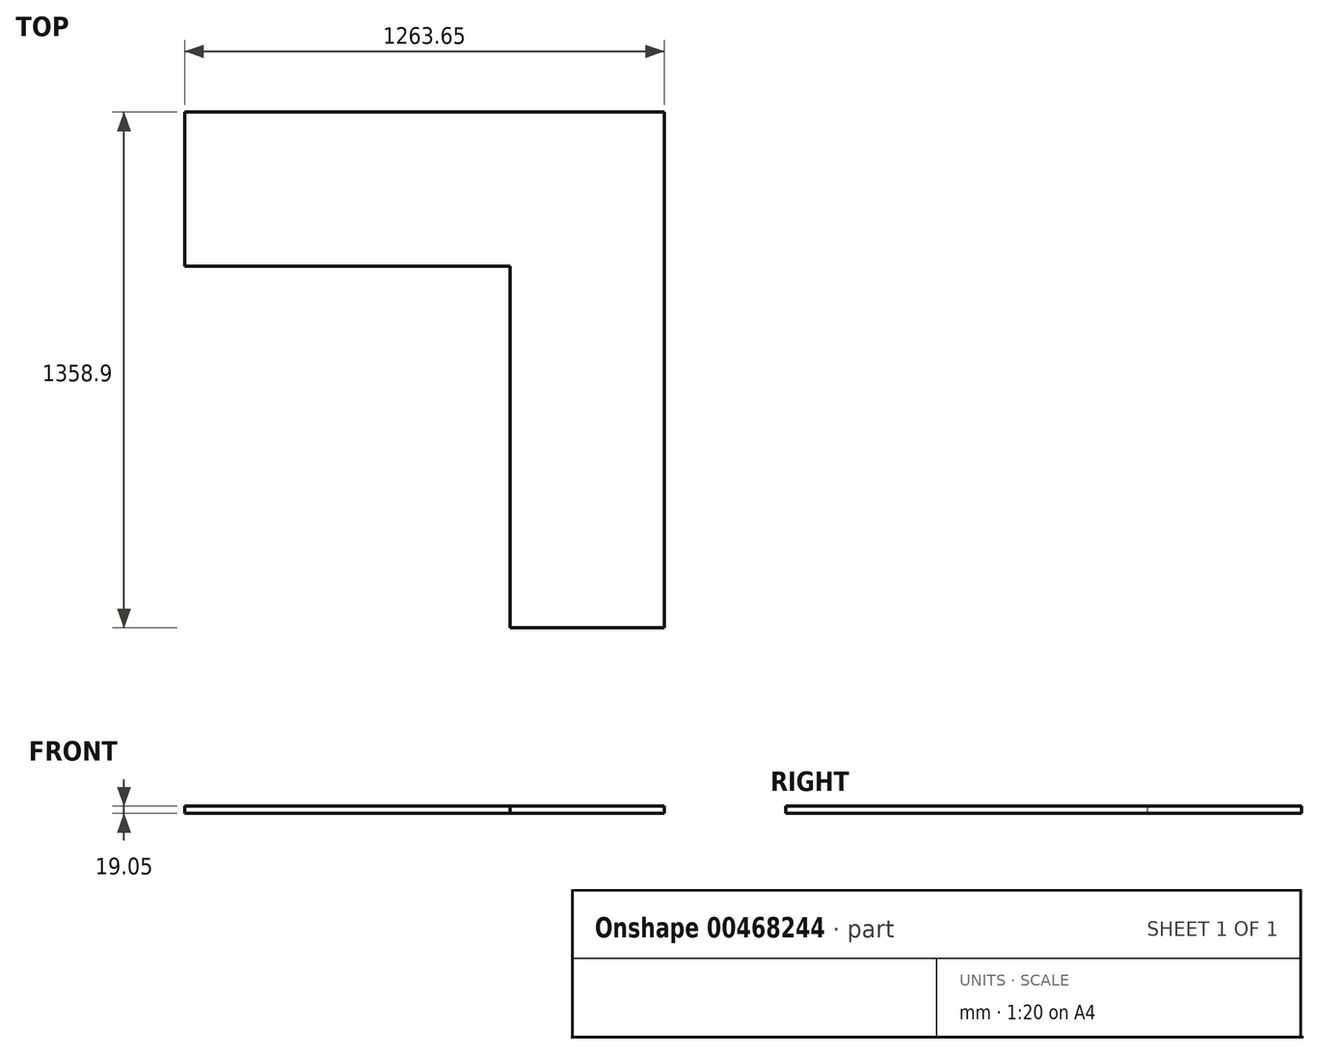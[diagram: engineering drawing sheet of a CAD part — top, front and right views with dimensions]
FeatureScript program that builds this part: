
annotation { "Feature Type Name" : "Feature", "Feature Type Description" : "" }
export const myFeature = defineFeature(function(context is Context, id is Id, definition is map)
    precondition{}
    {
        {
            var Q0;
            Q0=qCreatedBy(makeId("Top.planeOp"),FACE);
            var sketch = newSketch(context, id + "F0", { "sketchPlane" : qUnion([Q0])});
            skLineSegment(sketch, "E0", {"start": v(0, 0) * mm, "end": v(-1263.65, 0) * mm});
            skLineSegment(sketch, "E1", {"start": v(-1263.65, 0) * mm, "end": v(-1263.65, -406.4) * mm});
            skLineSegment(sketch, "E2", {"start": v(-406.4, -1358.9) * mm, "end": v(0, -1358.9) * mm});
            skLineSegment(sketch, "E3", {"start": v(0, -1358.9) * mm, "end": v(0, 0) * mm});
            skLineSegment(sketch, "E4", {"start": v(-1263.65, -406.4) * mm, "end": v(-406.4, -406.4) * mm});
            skLineSegment(sketch, "E5", {"start": v(-406.4, -406.4) * mm, "end": v(-406.4, -1358.9) * mm});
            skLineSegment(sketch, "E6.0", {"start": v(-1225.55, -38.1) * mm, "end": v(-1225.55, -406.4) * mm});
            skLineSegment(sketch, "E6.1", {"start": v(-38.1, -38.1) * mm, "end": v(-1225.55, -38.1) * mm});
            skLineSegment(sketch, "E6.2", {"start": v(-38.1, -1320.8) * mm, "end": v(-38.1, -38.1) * mm});
            skLineSegment(sketch, "E6.3", {"start": v(-406.4, -1320.8) * mm, "end": v(-38.1, -1320.8) * mm});
            skLineSegment(sketch, "E7", {"start": v(-1225.55, -406.4) * mm, "end": v(-1263.65, -406.4) * mm});
            skLineSegment(sketch, "E8", {"start": v(-406.4, -1320.8) * mm, "end": v(-406.4, -1358.9) * mm});
            skSolve(sketch);
        }
        {
            var Q0;
            Q0=qSketchRegion(id+"F0",true);
            extrude(context, id + "F1", {"entities" : qUnion([Q0]), "depth" : 19.05 * mm});
        }
    });
